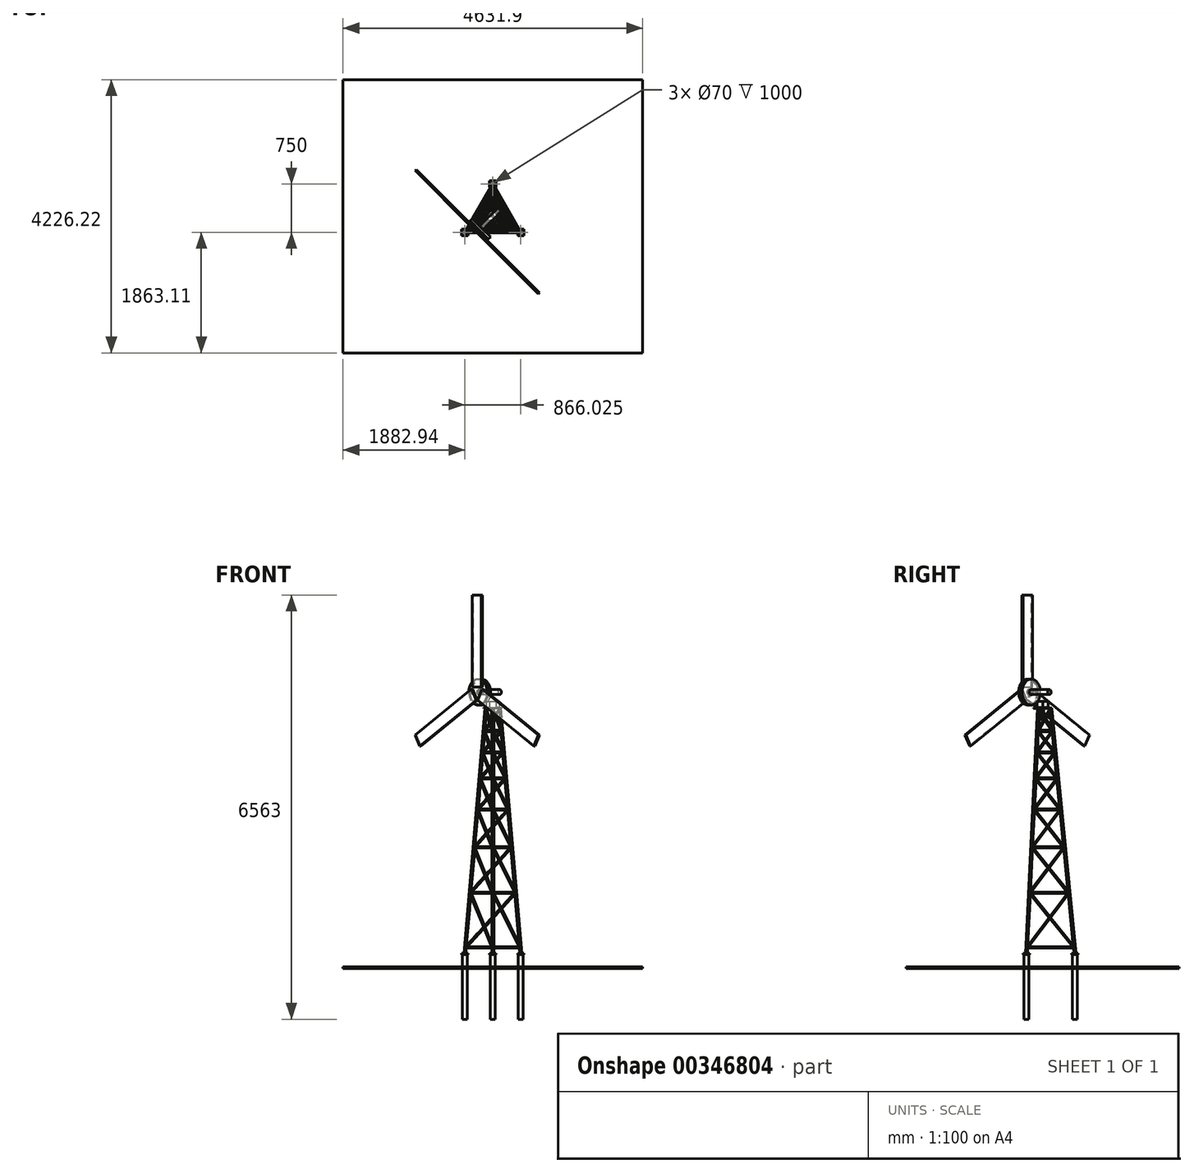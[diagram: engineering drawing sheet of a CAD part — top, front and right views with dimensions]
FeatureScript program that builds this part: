
annotation { "Feature Type Name" : "Feature", "Feature Type Description" : "" }
export const myFeature = defineFeature(function(context is Context, id is Id, definition is map)
    precondition{}
    {
        {
            assignVariable(context, id + "F0", {"name" : "RotorDia", "anyValue" : 3000});
        }
        {
            assignVariable(context, id + "F1", {"name" : "TowerHeight", "anyValue" : getVariable(context, 'RotorDia') / 2 + 2500});
        }
        {
            var Q0;
            Q0=qCreatedBy(makeId("Top.planeOp"),FACE);
            cPlane(context, id + "F2", {"entities" : qUnion([Q0]), "cplaneType" : CPlaneType.OFFSET, "offset" : 200 * mm, "width" : 150 * mm, "height" : 150 * mm});
        }
        {
            var Q0;
            Q0=qCreatedBy(id+"F2.planeOp",FACE);
            var sketch = newSketch(context, id + "F3", { "sketchPlane" : qUnion([Q0])});
            skLineSegment(sketch, "E0", {"start": v(0, 500) * mm, "end": v(-433.01, -250) * mm});
            skLineSegment(sketch, "E1", {"start": v(-433.01, -250) * mm, "end": v(433.01, -250) * mm});
            skLineSegment(sketch, "E2", {"start": v(433.01, -250) * mm, "end": v(0, 500) * mm});
            skLineSegment(sketch, "E3", {"start": v(-433.01, -250) * mm, "end": v(0, 0) * mm, "construction": true});
            skLineSegment(sketch, "E4", {"start": v(0, 0) * mm, "end": v(0, 500) * mm, "construction": true});
            skLineSegment(sketch, "E5", {"start": v(0, 0) * mm, "end": v(433.01, -250) * mm, "construction": true});
            skSolve(sketch);
        }
        {
            var Q0;
            Q0=qCreatedBy(makeId("Top.planeOp"),FACE);
            cPlane(context, id + "F4", {"entities" : qUnion([Q0]), "cplaneType" : CPlaneType.OFFSET, "offset" : (getVariable(context, 'TowerHeight')) * mm, "width" : 150 * mm, "height" : 150 * mm});
        }
        {
            var Q0;
            Q0=qCreatedBy(id+"F4.planeOp",FACE);
            var sketch = newSketch(context, id + "F5", { "sketchPlane" : qUnion([Q0])});
            skLineSegment(sketch, "E6", {"start": v(0, 125) * mm, "end": v(-108.25, -62.5) * mm});
            skLineSegment(sketch, "E7", {"start": v(-108.25, -62.5) * mm, "end": v(108.25, -62.5) * mm});
            skLineSegment(sketch, "E8", {"start": v(108.25, -62.5) * mm, "end": v(0, 125) * mm});
            skLineSegment(sketch, "E9", {"start": v(0, 125) * mm, "end": v(0, 0) * mm, "construction": true});
            skLineSegment(sketch, "E10", {"start": v(0, 0) * mm, "end": v(-108.25, -62.5) * mm, "construction": true});
            skLineSegment(sketch, "E11", {"start": v(108.25, -62.5) * mm, "end": v(0, 0) * mm, "construction": true});
            skSolve(sketch);
        }
        {
            var Q0;
            Q0=sQuery(id+"F3.wireOp",VERTEX,"E3.start");
            var Q1;
            Q1=sQuery(id+"F3.wireOp",VERTEX,"E5.end");
            var Q2;
            Q2=sQuery(id+"F5.wireOp",VERTEX,"E10.end");
            cPlane(context, id + "F6", {"entities" : qUnion([Q0, Q1, Q2]), "cplaneType" : CPlaneType.THREE_POINT, "offset" : 25 * mm, "width" : 150 * mm, "height" : 150 * mm});
        }
        {
            var Q0;
            Q0=qCreatedBy(id+"F6.planeOp",FACE);
            var sketch = newSketch(context, id + "F7", { "sketchPlane" : qUnion([Q0])});
            skLineSegment(sketch, "E12", {"start": v(433.01, 187.44) * mm, "end": v(108.25, 3992.06) * mm});
            skSolve(sketch);
        }
        {
            assignVariable(context, id + "F8", {"name" : "PipeThickness", "anyValue" : 3});
        }
        {
            var Q0;
            Q0=sQuery(id+"F7.wireOp",VERTEX,"E12.end");
            var Q1;
            Q1=sQuery(id+"F7.wireOp",EDGE,"E12");
            cPlane(context, id + "F9", {"entities" : qUnion([Q0, Q1]), "cplaneType" : CPlaneType.LINE_POINT, "offset" : 25 * mm, "width" : 150 * mm, "height" : 150 * mm});
        }
        {
            var Q0;
            Q0=qCreatedBy(id+"F9.planeOp",FACE);
            var sketch = newSketch(context, id + "F10", { "sketchPlane" : qUnion([Q0])});
            skCircle(sketch, "E13", {"center": v(-447.39, -259.55) * mm, "radius": 15 * mm});
            skSolve(sketch);
        }
        {
            var Q0;
            Q0=makeQuery(id+"F10.imprint","IMPRINT",FACE,{"disambiguationData":[TD([[makeQuery(id+"F10.imprint","IMPRINT",EDGE,{"derivedFrom":sQuery(id+"F10.wireOp",EDGE,"E13")}),1.0]])]});
            var Q1;
            Q1=sQuery(id+"F7.wireOp",EDGE,"E12");
            sweep(context, id + "F11", {"profiles" : qUnion([Q0]), "path" : qUnion([Q1])});
        }
        {
            var Q0;
            Q0=makeQuery(id+"F11.opSweep","CAP_FACE",FACE,{"disambiguationData":[OSD([sQuery(id+"F7.wireOp",VERTEX,"E12.end"),sQuery(id+"F10.wireOp",EDGE,"E13")])],"isStart":true});
            shell(context, id + "F12", {"entities" : qUnion([Q0]), "thickness" : (getVariable(context, 'PipeThickness')) * mm});
        }
        {
            var Q0;
            Q0=qCreatedBy(makeId("Front.planeOp"),FACE);
            var sketch = newSketch(context, id + "F13", { "sketchPlane" : qUnion([Q0])});
            skLineSegment(sketch, "E14", {"start": v(0, 0) * mm, "end": v(0, 4000) * mm});
            skSolve(sketch);
        }
        {
            var Q0;
            Q0=makeQuery(id+"F11.opSweep","SWEPT_BODY",BODY,{"disambiguationData":[OSD([sQuery(id+"F7.wireOp",EDGE,"E12"),sQuery(id+"F10.wireOp",EDGE,"E13")])]});
            var Q1;
            Q1=sQuery(id+"F13.wireOp",EDGE,"E14");
            transform(context, id + "F14", {"entities" : qUnion([Q0]), "transformType" : TransformType.ROTATION, "transformAxis" : qUnion([Q1]), "angle" : 120 * degree, "makeCopy" : true});
        }
        {
            var Q0;
            Q0=makeQuery(id+"F14.opPattern","COPY",BODY,{"derivedFrom":makeQuery(id+"F11.opSweep","SWEPT_BODY",BODY,{"disambiguationData":[OSD([sQuery(id+"F7.wireOp",EDGE,"E12"),sQuery(id+"F10.wireOp",EDGE,"E13")])]}),"instanceName":"1"});
            var Q1;
            Q1=sQuery(id+"F13.wireOp",EDGE,"E14");
            transform(context, id + "F15", {"entities" : qUnion([Q0]), "transformType" : TransformType.ROTATION, "transformAxis" : qUnion([Q1]), "angle" : 120 * degree, "makeCopy" : true});
        }
        {
            var Q0;
            Q0=qCreatedBy(id+"F4.planeOp",FACE);
            var sketch = newSketch(context, id + "F16", { "sketchPlane" : qUnion([Q0])});
            skCircle(sketch, "E15", {"center": v(0, 0) * mm, "radius": 139.93 * mm});
            skSolve(sketch);
        }
        {
            var Q0;
            Q0 = qSketchRegion(id + "F16", true);
            extrude(context, id + "F17", {"entities" : qUnion([Q0]), "depth" : 8 * mm});
        }
        {
            var Q0;
            Q0=makeQuery(id+"F17.opExtrude","CAP_FACE",FACE,{"disambiguationData":[OSD([sQuery(id+"F16.wireOp",EDGE,"E15")])],"isStart":false});
            var sketch = newSketch(context, id + "F18", { "sketchPlane" : qUnion([Q0])});
            skCircle(sketch, "E16", {"center": v(0, 0) * mm, "radius": 75 * mm});
            skCircle(sketch, "E17", {"center": v(0, 0) * mm, "radius": 80 * mm});
            skCircle(sketch, "E18", {"center": v(0, 0) * mm, "radius": 85 * mm});
            skCircle(sketch, "E19", {"center": v(0, 0) * mm, "radius": 90 * mm});
            skCircle(sketch, "E20", {"center": v(0, 0) * mm, "radius": 95 * mm});
            skCircle(sketch, "E21", {"center": v(0, 0) * mm, "radius": 100 * mm});
            skSolve(sketch);
        }
        {
            var Q0;
            Q0 = qSketchRegion(id + "F18", true);
            var Q1;
            Q1=makeQuery(id+"F18.imprint","IMPRINT",FACE,{"disambiguationData":[TD([[makeQuery(id+"F18.imprint","IMPRINT",EDGE,{"derivedFrom":sQuery(id+"F18.wireOp",EDGE,"E18")}),-1.0]])]});
            var Q2;
            Q2=makeQuery(id+"F18.imprint","IMPRINT",FACE,{"disambiguationData":[TD([[makeQuery(id+"F18.imprint","IMPRINT",EDGE,{"derivedFrom":sQuery(id+"F18.wireOp",EDGE,"E16")}),-1.0]])]});
            extrude(context, id + "F19", {"entities" : qUnion([Q0, Q1, Q2]), "depth" : 3 * mm});
        }
        {
            var Q0;
            Q0=makeQuery(id+"F17.opExtrude","CAP_FACE",FACE,{"disambiguationData":[OSD([sQuery(id+"F16.wireOp",EDGE,"E15")])],"isStart":false});
            var sketch = newSketch(context, id + "F20", { "sketchPlane" : qUnion([Q0])});
            skCircle(sketch, "E22", {"center": v(0, 0) * mm, "radius": 17.5 * mm});
            skSolve(sketch);
        }
        {
            var Q0;
            Q0 = qSketchRegion(id + "F20", true);
            extrude(context, id + "F21", {"entities" : qUnion([Q0]), "depth" : 25 * mm, "hasSecondDirection" : true, "secondDirectionOppositeDirection" : true, "secondDirectionDepth" : 200 * mm});
        }
        {
            var Q0;
            Q0=makeQuery(id+"F21.opExtrude","CAP_FACE",FACE,{"disambiguationData":[OSD([sQuery(id+"F20.wireOp",EDGE,"E22")])],"isStart":false});
            var sketch = newSketch(context, id + "F22", { "sketchPlane" : qUnion([Q0])});
            skCircle(sketch, "E23", {"center": v(0, 0) * mm, "radius": 60 * mm});
            skSolve(sketch);
        }
        {
            var Q0;
            Q0 = qSketchRegion(id + "F22", true);
            extrude(context, id + "F23", {"entities" : qUnion([Q0]), "operationType" : NewBodyOperationType.ADD, "depth" : 10 * mm});
        }
        {
            var Q0;
            Q0=makeQuery(id+"F23.opExtrude","CAP_FACE",FACE,{"disambiguationData":[OSD([sQuery(id+"F22.wireOp",EDGE,"E23")])],"isStart":false});
            var sketch = newSketch(context, id + "F24", { "sketchPlane" : qUnion([Q0])});
            skCircle(sketch, "E24.0", {"center": v(0, 0) * mm, "radius": 60 * mm});
            skSolve(sketch);
        }
        {
            var Q0;
            Q0 = qSketchRegion(id + "F24", true);
            extrude(context, id + "F25", {"entities" : qUnion([Q0]), "depth" : 10 * mm});
        }
        {
            var Q0;
            Q0=makeQuery(id+"F25.opExtrude","CAP_FACE",FACE,{"disambiguationData":[OSD([sQuery(id+"F24.wireOp",EDGE,"E24.0")])],"isStart":false});
            var sketch = newSketch(context, id + "F26", { "sketchPlane" : qUnion([Q0])});
            skPoint(sketch, "E25", {"position": v(0, 50) * mm});
            skPoint(sketch, "E26.1.0", {"position": v(-50, 0) * mm});
            skPoint(sketch, "E26.2.0", {"position": v(0, -50) * mm});
            skPoint(sketch, "E26.3.0", {"position": v(50, 0) * mm});
            skPoint(sketch, "E26.center", {"position": v(0, 0) * mm});
            skSolve(sketch);
        }
        {
            var Q0;
            Q0=sQuery(id+"F26.wireOp",VERTEX,"E25");
            var Q1;
            Q1=sQuery(id+"F26.wireOp",VERTEX,"E26.3.0");
            var Q2;
            Q2=sQuery(id+"F26.wireOp",VERTEX,"E26.2.0");
            var Q3;
            Q3=sQuery(id+"F26.wireOp",VERTEX,"E26.1.0");
            var Q4;
            Q4=makeQuery(id+"F25.opExtrude","SWEPT_BODY",BODY,{"disambiguationData":[OSD([sQuery(id+"F24.wireOp",EDGE,"E24.0")])]});
            var Q5;
            Q5=makeQuery(id+"F21.opExtrude","SWEPT_BODY",BODY,{"disambiguationData":[OSD([sQuery(id+"F20.wireOp",EDGE,"E22")])]});
            hole(context, id + "F27", {"style" : HoleStyle.SIMPLE, "endStyle" : HoleEndStyle.THROUGH, "standardTappedOrClearance" : lookupTablePath({ "standard" : "ISO", "fit" : "Close", "size" : "M12", "type" : "Clearance" }), "standardBlindInLast" : lookupTablePath({ "fit" : "Close", "standard" : "ISO", "size" : "M12", "type" : "Clearance" }), "holeDiameter" : 12.6 * mm, "isTappedThrough" : true, "tappedDepth" : 12 * mm, "tapClearance" : 3, "locations" : qUnion([Q0, Q1, Q2, Q3]), "scope" : qUnion([Q4, Q5])});
        }
        {
            var Q0;
            Q0=qCreatedBy(makeId("Front.planeOp"),FACE);
            var Q1;
            Q1=qCreatedBy(makeId("Right.planeOp"),FACE);
            cPlane(context, id + "F28", {"entities" : qUnion([Q0, Q1]), "cplaneType" : CPlaneType.MID_PLANE, "offset" : 25 * mm, "width" : 150 * mm, "height" : 150 * mm});
        }
        {
            var Q0;
            Q0=qCreatedBy(id+"F28.planeOp",FACE);
            var sketch = newSketch(context, id + "F29", { "sketchPlane" : qUnion([Q0])});
            skCircle(sketch, "E27", {"center": v(0, 4253) * mm, "radius": 38 * mm});
            skSolve(sketch);
        }
        {
            var Q0;
            Q0 = qSketchRegion(id + "F29", true);
            extrude(context, id + "F30", {"entities" : qUnion([Q0]), "depth" : 300 * mm, "hasSecondDirection" : true, "secondDirectionOppositeDirection" : true, "secondDirectionDepth" : 150 * mm});
        }
        {
            var Q0;
            Q0=makeQuery(id+"F30.opExtrude","CAP_FACE",FACE,{"disambiguationData":[OSD([sQuery(id+"F29.wireOp",EDGE,"E27")])],"isStart":false});
            var sketch = newSketch(context, id + "F31", { "sketchPlane" : qUnion([Q0])});
            skCircle(sketch, "E28", {"center": v(0, 4253) * mm, "radius": 200 * mm});
            skSolve(sketch);
        }
        {
            var Q0;
            Q0 = qSketchRegion(id + "F31", true);
            extrude(context, id + "F32", {"entities" : qUnion([Q0]), "depth" : 25 * mm});
        }
        {
            var Q0;
            Q0=makeQuery(id+"F32.opExtrude","CAP_FACE",FACE,{"disambiguationData":[OSD([sQuery(id+"F31.wireOp",EDGE,"E28")])],"isStart":true});
            cPlane(context, id + "F33", {"entities" : qUnion([Q0]), "cplaneType" : CPlaneType.OFFSET, "offset" : 1 * mm, "width" : 150 * mm, "height" : 150 * mm});
        }
        {
            var Q0;
            Q0=qCreatedBy(id+"F33.planeOp",FACE);
            var sketch = newSketch(context, id + "F34", { "sketchPlane" : qUnion([Q0])});
            skCircle(sketch, "E29.0", {"center": v(0, 4253) * mm, "radius": 200 * mm});
            skCircle(sketch, "E30", {"center": v(0, 4253) * mm, "radius": 43 * mm});
            skCircle(sketch, "E31.0", {"center": v(0, 4253) * mm, "radius": 38 * mm, "construction": true});
            skSolve(sketch);
        }
        {
            var Q0;
            Q0 = qSketchRegion(id + "F34", true);
            extrude(context, id + "F35", {"entities" : qUnion([Q0]), "depth" : 50 * mm});
        }
        {
            var Q0;
            Q0=makeQuery(id+"F32.opExtrude","CAP_FACE",FACE,{"disambiguationData":[OSD([sQuery(id+"F31.wireOp",EDGE,"E28")])],"isStart":false});
            var sketch = newSketch(context, id + "F36", { "sketchPlane" : qUnion([Q0])});
            skLineSegment(sketch, "E32", {"start": v(0, 4253) * mm, "end": v(0, 6624.87) * mm, "construction": true});
            skLineSegment(sketch, "E33.bottom", {"start": v(100, 4328) * mm, "end": v(-100, 4328) * mm});
            skLineSegment(sketch, "E33.top", {"start": v(100, 5753) * mm, "end": v(-100, 5753) * mm});
            skLineSegment(sketch, "E33.left", {"start": v(100, 4328) * mm, "end": v(100, 5753) * mm});
            skLineSegment(sketch, "E33.right", {"start": v(-100, 4328) * mm, "end": v(-100, 5753) * mm});
            skPoint(sketch, "E33.middle", {"position": v(0, 5040.5) * mm});
            skLineSegment(sketch, "E34.1.0", {"start": v(-114.95, 4302.1) * mm, "end": v(-14.95, 4128.9) * mm});
            skLineSegment(sketch, "E34.1.1", {"start": v(-114.95, 4302.1) * mm, "end": v(-1349.04, 3589.6) * mm});
            skLineSegment(sketch, "E34.1.2", {"start": v(-1349.04, 3589.6) * mm, "end": v(-1249.04, 3416.4) * mm});
            skLineSegment(sketch, "E34.1.3", {"start": v(-14.95, 4128.9) * mm, "end": v(-1249.04, 3416.4) * mm});
            skPoint(sketch, "E34.1.4", {"position": v(-682, 3859.25) * mm});
            skLineSegment(sketch, "E34.2.0", {"start": v(14.95, 4128.9) * mm, "end": v(114.95, 4302.1) * mm});
            skLineSegment(sketch, "E34.2.1", {"start": v(14.95, 4128.9) * mm, "end": v(1249.04, 3416.4) * mm});
            skLineSegment(sketch, "E34.2.2", {"start": v(1249.04, 3416.4) * mm, "end": v(1349.04, 3589.6) * mm});
            skLineSegment(sketch, "E34.2.3", {"start": v(114.95, 4302.1) * mm, "end": v(1349.04, 3589.6) * mm});
            skPoint(sketch, "E34.2.4", {"position": v(682, 3859.25) * mm});
            skPoint(sketch, "E34.center", {"position": v(0, 4253) * mm});
            skSolve(sketch);
        }
        {
            var Q0;
            Q0 = qSketchRegion(id + "F36", true);
            extrude(context, id + "F37", {"entities" : qUnion([Q0]), "depth" : 25 * mm});
        }
        {
            var Q0;
            Q0=qCreatedBy(makeId("Top.planeOp"),FACE);
            var sketch = newSketch(context, id + "F38", { "sketchPlane" : qUnion([Q0])});
            skLineSegment(sketch, "E35.bottom", {"start": v(2315.95, -2113.11) * mm, "end": v(-2315.95, -2113.11) * mm});
            skLineSegment(sketch, "E35.top", {"start": v(2315.95, 2113.11) * mm, "end": v(-2315.95, 2113.11) * mm});
            skLineSegment(sketch, "E35.left", {"start": v(2315.95, -2113.11) * mm, "end": v(2315.95, 2113.11) * mm});
            skLineSegment(sketch, "E35.right", {"start": v(-2315.95, -2113.11) * mm, "end": v(-2315.95, 2113.11) * mm});
            skPoint(sketch, "E35.middle", {"position": v(0, 0) * mm});
            skSolve(sketch);
        }
        {
            var Q0;
            Q0 = qSketchRegion(id + "F38", true);
            extrude(context, id + "F39", {"entities" : qUnion([Q0]), "oppositeDirection" : true, "depth" : 25 * mm});
        }
        {
            var Q0;
            Q0=qCreatedBy(id+"F2.planeOp",FACE);
            var sketch = newSketch(context, id + "F40", { "sketchPlane" : qUnion([Q0])});
            skLineSegment(sketch, "E36.bottom", {"start": v(383.01, -300) * mm, "end": v(483.01, -300) * mm});
            skLineSegment(sketch, "E36.top", {"start": v(383.01, -200) * mm, "end": v(483.01, -200) * mm});
            skLineSegment(sketch, "E36.left", {"start": v(383.01, -300) * mm, "end": v(383.01, -200) * mm});
            skLineSegment(sketch, "E36.right", {"start": v(483.01, -300) * mm, "end": v(483.01, -200) * mm});
            skPoint(sketch, "E36.middle", {"position": v(433.01, -250) * mm});
            skLineSegment(sketch, "E37.bottom", {"start": v(-483.01, -300) * mm, "end": v(-383.01, -300) * mm});
            skLineSegment(sketch, "E37.top", {"start": v(-483.01, -200) * mm, "end": v(-383.01, -200) * mm});
            skLineSegment(sketch, "E37.left", {"start": v(-483.01, -300) * mm, "end": v(-483.01, -200) * mm});
            skLineSegment(sketch, "E37.right", {"start": v(-383.01, -300) * mm, "end": v(-383.01, -200) * mm});
            skPoint(sketch, "E37.middle", {"position": v(-433.01, -250) * mm});
            skLineSegment(sketch, "E38.bottom", {"start": v(-50, 450) * mm, "end": v(50, 450) * mm});
            skLineSegment(sketch, "E38.top", {"start": v(-50, 550) * mm, "end": v(50, 550) * mm});
            skLineSegment(sketch, "E38.left", {"start": v(-50, 450) * mm, "end": v(-50, 550) * mm});
            skLineSegment(sketch, "E38.right", {"start": v(50, 450) * mm, "end": v(50, 550) * mm});
            skPoint(sketch, "E38.middle", {"position": v(0, 500) * mm});
            skSolve(sketch);
        }
        {
            var Q0;
            Q0 = qSketchRegion(id + "F40", true);
            extrude(context, id + "F41", {"entities" : qUnion([Q0]), "depth" : 10 * mm});
        }
        {
            var Q0;
            Q0=makeQuery(id+"F41.opExtrude","CAP_FACE",FACE,{"disambiguationData":[OSD([sQuery(id+"F40.wireOp",EDGE,"E38.bottom"),sQuery(id+"F40.wireOp",EDGE,"E38.top"),sQuery(id+"F40.wireOp",EDGE,"E38.left"),sQuery(id+"F40.wireOp",EDGE,"E38.right")])],"isStart":true});
            var sketch = newSketch(context, id + "F42", { "sketchPlane" : qUnion([Q0])});
            skLineSegment(sketch, "E39.0.0", {"start": v(-50, -550) * mm, "end": v(50, -550) * mm});
            skLineSegment(sketch, "E39.0.1", {"start": v(50, -550) * mm, "end": v(50, -450) * mm});
            skLineSegment(sketch, "E39.0.2", {"start": v(50, -450) * mm, "end": v(-50, -450) * mm});
            skLineSegment(sketch, "E39.0.3", {"start": v(-50, -450) * mm, "end": v(-50, -550) * mm});
            skLineSegment(sketch, "E40.0.0", {"start": v(383.01, 200) * mm, "end": v(483.01, 200) * mm});
            skLineSegment(sketch, "E40.0.1", {"start": v(483.01, 200) * mm, "end": v(483.01, 300) * mm});
            skLineSegment(sketch, "E40.0.2", {"start": v(483.01, 300) * mm, "end": v(383.01, 300) * mm});
            skLineSegment(sketch, "E40.0.3", {"start": v(383.01, 300) * mm, "end": v(383.01, 200) * mm});
            skLineSegment(sketch, "E41.0.0", {"start": v(-483.01, 200) * mm, "end": v(-383.01, 200) * mm});
            skLineSegment(sketch, "E41.0.1", {"start": v(-383.01, 200) * mm, "end": v(-383.01, 300) * mm});
            skLineSegment(sketch, "E41.0.2", {"start": v(-383.01, 300) * mm, "end": v(-483.01, 300) * mm});
            skLineSegment(sketch, "E41.0.3", {"start": v(-483.01, 300) * mm, "end": v(-483.01, 200) * mm});
            skSolve(sketch);
        }
        {
            var Q0;
            Q0 = qSketchRegion(id + "F42", true);
            extrude(context, id + "F43", {"entities" : qUnion([Q0]), "depth" : 10 * mm});
        }
        {
            var Q0;
            Q0=makeQuery(id+"F43.opExtrude","CAP_FACE",FACE,{"disambiguationData":[OSD([sQuery(id+"F42.wireOp",EDGE,"E39.0.0"),sQuery(id+"F42.wireOp",EDGE,"E39.0.1"),sQuery(id+"F42.wireOp",EDGE,"E39.0.2"),sQuery(id+"F42.wireOp",EDGE,"E39.0.3")])],"isStart":false});
            var sketch = newSketch(context, id + "F44", { "sketchPlane" : qUnion([Q0])});
            skCircle(sketch, "E42", {"center": v(0, -500) * mm, "radius": 38 * mm});
            skCircle(sketch, "E43", {"center": v(433.01, 250) * mm, "radius": 38 * mm});
            skCircle(sketch, "E44", {"center": v(-433.01, 250) * mm, "radius": 38 * mm});
            skCircle(sketch, "E45", {"center": v(0, -500) * mm, "radius": 35 * mm});
            skCircle(sketch, "E46", {"center": v(433.01, 250) * mm, "radius": 35 * mm});
            skCircle(sketch, "E47", {"center": v(-433.01, 250) * mm, "radius": 35 * mm});
            skSolve(sketch);
        }
        {
            var Q0;
            Q0 = qSketchRegion(id + "F44", true);
            extrude(context, id + "F45", {"entities" : qUnion([Q0]), "depth" : 1000 * mm});
        }
        {
            var Q0;
            Q0=qCreatedBy(id+"F6.planeOp",FACE);
            var sketch = newSketch(context, id + "F46", { "sketchPlane" : qUnion([Q0])});
            skLineSegment(sketch, "E48", {"start": v(433.01, 194.96) * mm, "end": v(108.25, 3992.06) * mm, "construction": true});
            skLineSegment(sketch, "E49", {"start": v(-433.01, 184.97) * mm, "end": v(-108.25, 3992.06) * mm, "construction": true});
            skLineSegment(sketch, "E50", {"start": v(425.1, 287.44) * mm, "end": v(-424.27, 287.44) * mm, "construction": true});
            skLineSegment(sketch, "E51", {"start": v(352.46, 1136.81) * mm, "end": v(-351.82, 1136.81) * mm, "construction": true});
            skLineSegment(sketch, "E52", {"start": v(292.22, 1841.09) * mm, "end": v(-291.74, 1841.09) * mm, "construction": true});
            skLineSegment(sketch, "E53", {"start": v(242.28, 2425.05) * mm, "end": v(-241.93, 2425.05) * mm, "construction": true});
            skLineSegment(sketch, "E54", {"start": v(200.86, 2909.25) * mm, "end": v(-200.62, 2909.25) * mm, "construction": true});
            skLineSegment(sketch, "E55", {"start": v(166.53, 3310.74) * mm, "end": v(-166.37, 3310.74) * mm, "construction": true});
            skLineSegment(sketch, "E56", {"start": v(138.05, 3643.63) * mm, "end": v(-137.98, 3643.63) * mm, "construction": true});
            skLineSegment(sketch, "E57", {"start": v(144.63, 287.44) * mm, "end": v(144.63, 1136.81) * mm, "construction": true});
            skLineSegment(sketch, "E58", {"start": v(-119.67, 1136.81) * mm, "end": v(-119.67, 1841.09) * mm, "construction": true});
            skLineSegment(sketch, "E59", {"start": v(112.4, 1841.09) * mm, "end": v(112.4, 2425.05) * mm, "construction": true});
            skLineSegment(sketch, "E60", {"start": v(-67.21, 2425.05) * mm, "end": v(-67.21, 2909.25) * mm, "construction": true});
            skLineSegment(sketch, "E61", {"start": v(72.8, 2909.25) * mm, "end": v(72.8, 3310.74) * mm, "construction": true});
            skLineSegment(sketch, "E62", {"start": v(-67.21, 3310.74) * mm, "end": v(-67.21, 3643.63) * mm, "construction": true});
            skSolve(sketch);
        }
        {
            var Q0;
            Q0=qCreatedBy(makeId("Right.planeOp"),FACE);
            var sketch = newSketch(context, id + "F47", { "sketchPlane" : qUnion([Q0])});
            skCircle(sketch, "E63", {"center": v(-245.07, 299.88) * mm, "radius": 10 * mm});
            skCircle(sketch, "E64", {"center": v(-203.21, 1148.22) * mm, "radius": 10 * mm});
            skCircle(sketch, "E65", {"center": v(-168.5, 1851.64) * mm, "radius": 10 * mm});
            skCircle(sketch, "E66", {"center": v(-139.73, 2434.9) * mm, "radius": 10 * mm});
            skCircle(sketch, "E67", {"center": v(-115.86, 2918.5) * mm, "radius": 10 * mm});
            skLineSegment(sketch, "E68", {"start": v(-250, 200) * mm, "end": v(-62.5, 4000) * mm, "construction": true});
            skCircle(sketch, "E69", {"center": v(-96.08, 3319.5) * mm, "radius": 10 * mm});
            skCircle(sketch, "E70", {"center": v(-79.67, 3652) * mm, "radius": 10 * mm});
            skCircle(sketch, "E71", {"center": v(-79.67, 3652) * mm, "radius": 8 * mm});
            skCircle(sketch, "E72", {"center": v(-96.08, 3319.5) * mm, "radius": 8 * mm});
            skCircle(sketch, "E73", {"center": v(-115.86, 2918.5) * mm, "radius": 8 * mm});
            skCircle(sketch, "E74", {"center": v(-139.73, 2434.9) * mm, "radius": 8 * mm});
            skCircle(sketch, "E75", {"center": v(-168.5, 1851.64) * mm, "radius": 8 * mm});
            skCircle(sketch, "E76", {"center": v(-203.21, 1148.22) * mm, "radius": 8 * mm});
            skCircle(sketch, "E77", {"center": v(-245.07, 299.88) * mm, "radius": 8 * mm});
            skSolve(sketch);
        }
        {
            var Q0;
            Q0 = qSketchRegion(id + "F47", true);
            extrude(context, id + "F48", {"entities" : qUnion([Q0]), "endBound" : BoundingType.UP_TO_NEXT, "depth" : 25 * mm, "hasSecondDirection" : true, "secondDirectionBound" : SecondDirectionBoundingType.UP_TO_NEXT, "secondDirectionOppositeDirection" : true, "secondDirectionDepth" : 25 * mm});
        }
        {
            var Q0;
            Q0=qCreatedBy(id+"F6.planeOp",FACE);
            var sketch = newSketch(context, id + "F49", { "sketchPlane" : qUnion([Q0])});
            skLineSegment(sketch, "E78", {"start": v(-337.77, 1126.81) * mm, "end": v(408.57, 297.44) * mm, "construction": true});
            skLineSegment(sketch, "E79", {"start": v(408.57, 297.44) * mm, "end": v(-71.24, 830.63) * mm});
            skSolve(sketch);
        }
        {
            var Q0;
            Q0=sQuery(id+"F49.wireOp",EDGE,"E79");
            var Q1;
            Q1=sQuery(id+"F49.wireOp",VERTEX,"E79.end");
            cPlane(context, id + "F50", {"entities" : qUnion([Q0, Q1]), "cplaneType" : CPlaneType.LINE_POINT, "offset" : 25 * mm, "width" : 150 * mm, "height" : 150 * mm});
        }
        {
            var Q0;
            Q0=qCreatedBy(id+"F50.planeOp",FACE);
            var sketch = newSketch(context, id + "F51", { "sketchPlane" : qUnion([Q0])});
            skCircle(sketch, "E80", {"center": v(-502.66, -259.55) * mm, "radius": 10 * mm});
            skCircle(sketch, "E81", {"center": v(-502.66, -259.55) * mm, "radius": 8 * mm});
            skSolve(sketch);
        }
        {
            var Q0;
            Q0 = qSketchRegion(id + "F51", true);
            var Q1;
            Q1=makeQuery(id+"F14.opPattern","COPY",BODY,{"derivedFrom":makeQuery(id+"F11.opSweep","SWEPT_BODY",BODY,{"disambiguationData":[OSD([sQuery(id+"F7.wireOp",EDGE,"E12"),sQuery(id+"F10.wireOp",EDGE,"E13")])]}),"instanceName":"1"});
            var Q2;
            Q2=makeQuery(id+"F11.opSweep","SWEPT_BODY",BODY,{"disambiguationData":[OSD([sQuery(id+"F7.wireOp",EDGE,"E12"),sQuery(id+"F10.wireOp",EDGE,"E13")])]});
            extrude(context, id + "F52", {"entities" : qUnion([Q0]), "endBound" : BoundingType.UP_TO_BODY, "endBoundEntityBody" : qUnion([Q1]), "depth" : 25 * mm, "hasSecondDirection" : true, "secondDirectionBound" : SecondDirectionBoundingType.UP_TO_BODY, "secondDirectionOppositeDirection" : true, "secondDirectionBoundEntityBody" : qUnion([Q2]), "secondDirectionDepth" : 25 * mm});
        }
        {
            var Q0;
            Q0=qCreatedBy(id+"F6.planeOp",FACE);
            var sketch = newSketch(context, id + "F53", { "sketchPlane" : qUnion([Q0])});
            skLineSegment(sketch, "E82", {"start": v(336.07, 1146.81) * mm, "end": v(-277.66, 1831.09) * mm, "construction": true});
            skLineSegment(sketch, "E83", {"start": v(336.07, 1146.81) * mm, "end": v(116.17, 1391.98) * mm});
            skSolve(sketch);
        }
        {
            var Q0;
            Q0=sQuery(id+"F53.wireOp",VERTEX,"E83.end");
            var Q1;
            Q1=sQuery(id+"F53.wireOp",EDGE,"E83");
            cPlane(context, id + "F54", {"entities" : qUnion([Q0, Q1]), "cplaneType" : CPlaneType.LINE_POINT, "offset" : 25 * mm, "width" : 150 * mm, "height" : 150 * mm});
        }
        {
            var Q0;
            Q0=qCreatedBy(id+"F54.planeOp",FACE);
            var sketch = newSketch(context, id + "F55", { "sketchPlane" : qUnion([Q0])});
            skCircle(sketch, "E84", {"center": v(-1015.9, -259.55) * mm, "radius": 10 * mm});
            skCircle(sketch, "E85", {"center": v(-1015.9, -259.55) * mm, "radius": 8 * mm});
            skSolve(sketch);
        }
        {
            var Q0;
            Q0 = qSketchRegion(id + "F55", true);
            var Q1;
            Q1=makeQuery(id+"F14.opPattern","COPY",BODY,{"derivedFrom":makeQuery(id+"F11.opSweep","SWEPT_BODY",BODY,{"disambiguationData":[OSD([sQuery(id+"F7.wireOp",EDGE,"E12"),sQuery(id+"F10.wireOp",EDGE,"E13")])]}),"instanceName":"1"});
            var Q2;
            Q2=makeQuery(id+"F11.opSweep","SWEPT_BODY",BODY,{"disambiguationData":[OSD([sQuery(id+"F7.wireOp",EDGE,"E12"),sQuery(id+"F10.wireOp",EDGE,"E13")])]});
            extrude(context, id + "F56", {"entities" : qUnion([Q0]), "endBound" : BoundingType.UP_TO_BODY, "endBoundEntityBody" : qUnion([Q1]), "depth" : 25 * mm, "hasSecondDirection" : true, "secondDirectionBound" : SecondDirectionBoundingType.UP_TO_BODY, "secondDirectionOppositeDirection" : true, "secondDirectionBoundEntityBody" : qUnion([Q2]), "secondDirectionDepth" : 25 * mm});
        }
        {
            var Q0;
            Q0=qCreatedBy(id+"F6.planeOp",FACE);
            var sketch = newSketch(context, id + "F57", { "sketchPlane" : qUnion([Q0])});
            skLineSegment(sketch, "E86", {"start": v(275.95, 1851.09) * mm, "end": v(-227.81, 2415.05) * mm, "construction": true});
            skLineSegment(sketch, "E87", {"start": v(275.95, 1851.09) * mm, "end": v(49.73, 2104.34) * mm});
            skSolve(sketch);
        }
        {
            var Q0;
            Q0=sQuery(id+"F57.wireOp",VERTEX,"E87.end");
            var Q1;
            Q1=sQuery(id+"F57.wireOp",EDGE,"E87");
            cPlane(context, id + "F58", {"entities" : qUnion([Q0, Q1]), "cplaneType" : CPlaneType.LINE_POINT, "offset" : 25 * mm, "width" : 150 * mm, "height" : 150 * mm});
        }
        {
            var Q0;
            Q0=qCreatedBy(id+"F58.planeOp",FACE);
            var sketch = newSketch(context, id + "F59", { "sketchPlane" : qUnion([Q0])});
            skCircle(sketch, "E88", {"center": v(-1438.96, -259.55) * mm, "radius": 10 * mm});
            skCircle(sketch, "E89", {"center": v(-1438.96, -259.55) * mm, "radius": 8 * mm});
            skSolve(sketch);
        }
        {
            var Q0;
            Q0 = qSketchRegion(id + "F59", true);
            var Q1;
            Q1=makeQuery(id+"F14.opPattern","COPY",BODY,{"derivedFrom":makeQuery(id+"F11.opSweep","SWEPT_BODY",BODY,{"disambiguationData":[OSD([sQuery(id+"F7.wireOp",EDGE,"E12"),sQuery(id+"F10.wireOp",EDGE,"E13")])]}),"instanceName":"1"});
            var Q2;
            Q2=makeQuery(id+"F11.opSweep","SWEPT_BODY",BODY,{"disambiguationData":[OSD([sQuery(id+"F7.wireOp",EDGE,"E12"),sQuery(id+"F10.wireOp",EDGE,"E13")])]});
            extrude(context, id + "F60", {"entities" : qUnion([Q0]), "endBound" : BoundingType.UP_TO_BODY, "endBoundEntityBody" : qUnion([Q1]), "depth" : 25 * mm, "hasSecondDirection" : true, "secondDirectionBound" : SecondDirectionBoundingType.UP_TO_BODY, "secondDirectionOppositeDirection" : true, "secondDirectionBoundEntityBody" : qUnion([Q2]), "secondDirectionDepth" : 25 * mm});
        }
        {
            var Q0;
            Q0=qCreatedBy(id+"F6.planeOp",FACE);
            var sketch = newSketch(context, id + "F61", { "sketchPlane" : qUnion([Q0])});
            skLineSegment(sketch, "E90", {"start": v(226.1, 2435.05) * mm, "end": v(-186.48, 2899.25) * mm, "construction": true});
            skLineSegment(sketch, "E91", {"start": v(226.1, 2435.05) * mm, "end": v(47.16, 2636.38) * mm});
            skSolve(sketch);
        }
        {
            var Q0;
            Q0=sQuery(id+"F61.wireOp",VERTEX,"E91.end");
            var Q1;
            Q1=sQuery(id+"F61.wireOp",EDGE,"E91");
            cPlane(context, id + "F62", {"entities" : qUnion([Q0, Q1]), "cplaneType" : CPlaneType.LINE_POINT, "offset" : 25 * mm, "width" : 150 * mm, "height" : 150 * mm});
        }
        {
            var Q0;
            Q0=qCreatedBy(id+"F62.planeOp",FACE);
            var sketch = newSketch(context, id + "F63", { "sketchPlane" : qUnion([Q0])});
            skCircle(sketch, "E92", {"center": v(-1786.67, -259.55) * mm, "radius": 10 * mm});
            skCircle(sketch, "E93", {"center": v(-1786.67, -259.55) * mm, "radius": 8 * mm});
            skSolve(sketch);
        }
        {
            var Q0;
            Q0 = qSketchRegion(id + "F63", true);
            var Q1;
            Q1=makeQuery(id+"F14.opPattern","COPY",BODY,{"derivedFrom":makeQuery(id+"F11.opSweep","SWEPT_BODY",BODY,{"disambiguationData":[OSD([sQuery(id+"F7.wireOp",EDGE,"E12"),sQuery(id+"F10.wireOp",EDGE,"E13")])]}),"instanceName":"1"});
            var Q2;
            Q2=makeQuery(id+"F11.opSweep","SWEPT_BODY",BODY,{"disambiguationData":[OSD([sQuery(id+"F7.wireOp",EDGE,"E12"),sQuery(id+"F10.wireOp",EDGE,"E13")])]});
            extrude(context, id + "F64", {"entities" : qUnion([Q0]), "endBound" : BoundingType.UP_TO_BODY, "endBoundEntityBody" : qUnion([Q1]), "depth" : 25 * mm, "hasSecondDirection" : true, "secondDirectionBound" : SecondDirectionBoundingType.UP_TO_BODY, "secondDirectionOppositeDirection" : true, "secondDirectionBoundEntityBody" : qUnion([Q2]), "secondDirectionDepth" : 25 * mm});
        }
        {
            var Q0;
            Q0=qCreatedBy(id+"F6.planeOp",FACE);
            var sketch = newSketch(context, id + "F65", { "sketchPlane" : qUnion([Q0])});
            skLineSegment(sketch, "E94", {"start": v(184.77, 2919.25) * mm, "end": v(-152.2, 3300.74) * mm, "construction": true});
            skLineSegment(sketch, "E95", {"start": v(184.77, 2919.25) * mm, "end": v(47.85, 3074.26) * mm});
            skSolve(sketch);
        }
        {
            var Q0;
            Q0=sQuery(id+"F65.wireOp",VERTEX,"E95.end");
            var Q1;
            Q1=sQuery(id+"F65.wireOp",EDGE,"E95");
            cPlane(context, id + "F66", {"entities" : qUnion([Q0, Q1]), "cplaneType" : CPlaneType.LINE_POINT, "offset" : 25 * mm, "width" : 150 * mm, "height" : 150 * mm});
        }
        {
            var Q0;
            Q0=qCreatedBy(id+"F66.planeOp",FACE);
            var sketch = newSketch(context, id + "F67", { "sketchPlane" : qUnion([Q0])});
            skCircle(sketch, "E96", {"center": v(-2071.14, -259.55) * mm, "radius": 10 * mm});
            skCircle(sketch, "E97", {"center": v(-2071.14, -259.55) * mm, "radius": 8 * mm});
            skSolve(sketch);
        }
        {
            var Q0;
            Q0 = qSketchRegion(id + "F67", true);
            var Q1;
            Q1=makeQuery(id+"F14.opPattern","COPY",BODY,{"derivedFrom":makeQuery(id+"F11.opSweep","SWEPT_BODY",BODY,{"disambiguationData":[OSD([sQuery(id+"F7.wireOp",EDGE,"E12"),sQuery(id+"F10.wireOp",EDGE,"E13")])]}),"instanceName":"1"});
            var Q2;
            Q2=makeQuery(id+"F11.opSweep","SWEPT_BODY",BODY,{"disambiguationData":[OSD([sQuery(id+"F7.wireOp",EDGE,"E12"),sQuery(id+"F10.wireOp",EDGE,"E13")])]});
            extrude(context, id + "F68", {"entities" : qUnion([Q0]), "endBound" : BoundingType.UP_TO_BODY, "endBoundEntityBody" : qUnion([Q1]), "depth" : 25 * mm, "hasSecondDirection" : true, "secondDirectionBound" : SecondDirectionBoundingType.UP_TO_BODY, "secondDirectionOppositeDirection" : true, "secondDirectionBoundEntityBody" : qUnion([Q2]), "secondDirectionDepth" : 25 * mm});
        }
        {
            var Q0;
            Q0=qCreatedBy(id+"F6.planeOp",FACE);
            var sketch = newSketch(context, id + "F69", { "sketchPlane" : qUnion([Q0])});
            skLineSegment(sketch, "E98", {"start": v(150.5, 3320.74) * mm, "end": v(-123.8, 3633.63) * mm, "construction": true});
            skLineSegment(sketch, "E99", {"start": v(150.5, 3320.74) * mm, "end": v(34.32, 3453.27) * mm});
            skSolve(sketch);
        }
        {
            var Q0;
            Q0=sQuery(id+"F69.wireOp",VERTEX,"E99.end");
            var Q1;
            Q1=sQuery(id+"F69.wireOp",EDGE,"E99");
            cPlane(context, id + "F70", {"entities" : qUnion([Q0, Q1]), "cplaneType" : CPlaneType.LINE_POINT, "offset" : 25 * mm, "width" : 150 * mm, "height" : 150 * mm});
        }
        {
            var Q0;
            Q0=qCreatedBy(id+"F70.planeOp",FACE);
            var sketch = newSketch(context, id + "F71", { "sketchPlane" : qUnion([Q0])});
            skCircle(sketch, "E100", {"center": v(-2302.2, -259.55) * mm, "radius": 10 * mm});
            skCircle(sketch, "E101", {"center": v(-2302.2, -259.55) * mm, "radius": 8 * mm});
            skSolve(sketch);
        }
        {
            var Q0;
            Q0 = qSketchRegion(id + "F71", true);
            var Q1;
            Q1=makeQuery(id+"F14.opPattern","COPY",BODY,{"derivedFrom":makeQuery(id+"F11.opSweep","SWEPT_BODY",BODY,{"disambiguationData":[OSD([sQuery(id+"F7.wireOp",EDGE,"E12"),sQuery(id+"F10.wireOp",EDGE,"E13")])]}),"instanceName":"1"});
            var Q2;
            Q2=makeQuery(id+"F11.opSweep","SWEPT_BODY",BODY,{"disambiguationData":[OSD([sQuery(id+"F7.wireOp",EDGE,"E12"),sQuery(id+"F10.wireOp",EDGE,"E13")])]});
            extrude(context, id + "F72", {"entities" : qUnion([Q0]), "endBound" : BoundingType.UP_TO_BODY, "endBoundEntityBody" : qUnion([Q1]), "depth" : 25 * mm, "hasSecondDirection" : true, "secondDirectionBound" : SecondDirectionBoundingType.UP_TO_BODY, "secondDirectionOppositeDirection" : true, "secondDirectionBoundEntityBody" : qUnion([Q2]), "secondDirectionDepth" : 25 * mm});
        }
        {
            var Q0;
            Q0=qCreatedBy(id+"F6.planeOp",FACE);
            var sketch = newSketch(context, id + "F73", { "sketchPlane" : qUnion([Q0])});
            skLineSegment(sketch, "E102", {"start": v(122.09, 3653.63) * mm, "end": v(-108.25, 3992.06) * mm, "construction": true});
            skLineSegment(sketch, "E103", {"start": v(122.09, 3653.63) * mm, "end": v(43.9, 3768.52) * mm});
            skSolve(sketch);
        }
        {
            var Q0;
            Q0=sQuery(id+"F73.wireOp",VERTEX,"E103.end");
            var Q1;
            Q1=sQuery(id+"F73.wireOp",EDGE,"E103");
            cPlane(context, id + "F74", {"entities" : qUnion([Q0, Q1]), "cplaneType" : CPlaneType.LINE_POINT, "offset" : 25 * mm, "width" : 150 * mm, "height" : 150 * mm});
        }
        {
            var Q0;
            Q0=qCreatedBy(id+"F74.planeOp",FACE);
            var sketch = newSketch(context, id + "F75", { "sketchPlane" : qUnion([Q0])});
            skCircle(sketch, "E104", {"center": v(-2156.69, -259.55) * mm, "radius": 10 * mm});
            skCircle(sketch, "E105", {"center": v(-2156.69, -259.55) * mm, "radius": 8 * mm});
            skSolve(sketch);
        }
        {
            var Q0;
            Q0 = qSketchRegion(id + "F75", true);
            var Q1;
            Q1=makeQuery(id+"F14.opPattern","COPY",BODY,{"derivedFrom":makeQuery(id+"F11.opSweep","SWEPT_BODY",BODY,{"disambiguationData":[OSD([sQuery(id+"F7.wireOp",EDGE,"E12"),sQuery(id+"F10.wireOp",EDGE,"E13")])]}),"instanceName":"1"});
            var Q2;
            Q2=makeQuery(id+"F11.opSweep","SWEPT_BODY",BODY,{"disambiguationData":[OSD([sQuery(id+"F7.wireOp",EDGE,"E12"),sQuery(id+"F10.wireOp",EDGE,"E13")])]});
            extrude(context, id + "F76", {"entities" : qUnion([Q0]), "endBound" : BoundingType.UP_TO_BODY, "endBoundEntityBody" : qUnion([Q1]), "depth" : 25 * mm, "hasSecondDirection" : true, "secondDirectionBound" : SecondDirectionBoundingType.UP_TO_BODY, "secondDirectionOppositeDirection" : true, "secondDirectionBoundEntityBody" : qUnion([Q2]), "secondDirectionDepth" : 25 * mm});
        }
        {
            var Q0;
            Q0=makeQuery(id+"F76.opExtrude","SWEPT_BODY",BODY,{"disambiguationData":[OSD([sQuery(id+"F75.wireOp",EDGE,"E104"),sQuery(id+"F75.wireOp",EDGE,"E105")])]});
            var Q1;
            Q1=makeQuery(id+"F48.opExtrude","SWEPT_BODY",BODY,{"disambiguationData":[OSD([sQuery(id+"F47.wireOp",EDGE,"E70"),sQuery(id+"F47.wireOp",EDGE,"E71")])]});
            var Q2;
            Q2=makeQuery(id+"F72.opExtrude","SWEPT_BODY",BODY,{"disambiguationData":[OSD([sQuery(id+"F71.wireOp",EDGE,"E100"),sQuery(id+"F71.wireOp",EDGE,"E101")])]});
            var Q3;
            Q3=makeQuery(id+"F48.opExtrude","SWEPT_BODY",BODY,{"disambiguationData":[OSD([sQuery(id+"F47.wireOp",EDGE,"E69"),sQuery(id+"F47.wireOp",EDGE,"E72")])]});
            var Q4;
            Q4=makeQuery(id+"F68.opExtrude","SWEPT_BODY",BODY,{"disambiguationData":[OSD([sQuery(id+"F67.wireOp",EDGE,"E96"),sQuery(id+"F67.wireOp",EDGE,"E97")])]});
            var Q5;
            Q5=makeQuery(id+"F48.opExtrude","SWEPT_BODY",BODY,{"disambiguationData":[OSD([sQuery(id+"F47.wireOp",EDGE,"E67"),sQuery(id+"F47.wireOp",EDGE,"E73")])]});
            var Q6;
            Q6=makeQuery(id+"F64.opExtrude","SWEPT_BODY",BODY,{"disambiguationData":[OSD([sQuery(id+"F63.wireOp",EDGE,"E92"),sQuery(id+"F63.wireOp",EDGE,"E93")])]});
            var Q7;
            Q7=makeQuery(id+"F48.opExtrude","SWEPT_BODY",BODY,{"disambiguationData":[OSD([sQuery(id+"F47.wireOp",EDGE,"E66"),sQuery(id+"F47.wireOp",EDGE,"E74")])]});
            var Q8;
            Q8=makeQuery(id+"F60.opExtrude","SWEPT_BODY",BODY,{"disambiguationData":[OSD([sQuery(id+"F59.wireOp",EDGE,"E88"),sQuery(id+"F59.wireOp",EDGE,"E89")])]});
            var Q9;
            Q9=makeQuery(id+"F48.opExtrude","SWEPT_BODY",BODY,{"disambiguationData":[OSD([sQuery(id+"F47.wireOp",EDGE,"E65"),sQuery(id+"F47.wireOp",EDGE,"E75")])]});
            var Q10;
            Q10=makeQuery(id+"F56.opExtrude","SWEPT_BODY",BODY,{"disambiguationData":[OSD([sQuery(id+"F55.wireOp",EDGE,"E84"),sQuery(id+"F55.wireOp",EDGE,"E85")])]});
            var Q11;
            Q11=makeQuery(id+"F48.opExtrude","SWEPT_BODY",BODY,{"disambiguationData":[OSD([sQuery(id+"F47.wireOp",EDGE,"E64"),sQuery(id+"F47.wireOp",EDGE,"E76")])]});
            var Q12;
            Q12=makeQuery(id+"F52.opExtrude","SWEPT_BODY",BODY,{"disambiguationData":[OSD([sQuery(id+"F51.wireOp",EDGE,"E80"),sQuery(id+"F51.wireOp",EDGE,"E81")])]});
            var Q13;
            Q13=makeQuery(id+"F48.opExtrude","SWEPT_BODY",BODY,{"disambiguationData":[OSD([sQuery(id+"F47.wireOp",EDGE,"E63"),sQuery(id+"F47.wireOp",EDGE,"E77")])]});
            var Q14;
            Q14=sQuery(id+"F13.wireOp",EDGE,"E14");
            transform(context, id + "F77", {"entities" : qUnion([Q0, Q1, Q2, Q3, Q4, Q5, Q6, Q7, Q8, Q9, Q10, Q11, Q12, Q13]), "transformType" : TransformType.ROTATION, "transformAxis" : qUnion([Q14]), "angle" : 120 * degree, "makeCopy" : true});
        }
        {
            var Q0;
            Q0=makeQuery(id+"F76.opExtrude","SWEPT_BODY",BODY,{"disambiguationData":[OSD([sQuery(id+"F75.wireOp",EDGE,"E104"),sQuery(id+"F75.wireOp",EDGE,"E105")])]});
            var Q1;
            Q1=makeQuery(id+"F48.opExtrude","SWEPT_BODY",BODY,{"disambiguationData":[OSD([sQuery(id+"F47.wireOp",EDGE,"E70"),sQuery(id+"F47.wireOp",EDGE,"E71")])]});
            var Q2;
            Q2=makeQuery(id+"F72.opExtrude","SWEPT_BODY",BODY,{"disambiguationData":[OSD([sQuery(id+"F71.wireOp",EDGE,"E100"),sQuery(id+"F71.wireOp",EDGE,"E101")])]});
            var Q3;
            Q3=makeQuery(id+"F48.opExtrude","SWEPT_BODY",BODY,{"disambiguationData":[OSD([sQuery(id+"F47.wireOp",EDGE,"E69"),sQuery(id+"F47.wireOp",EDGE,"E72")])]});
            var Q4;
            Q4=makeQuery(id+"F68.opExtrude","SWEPT_BODY",BODY,{"disambiguationData":[OSD([sQuery(id+"F67.wireOp",EDGE,"E96"),sQuery(id+"F67.wireOp",EDGE,"E97")])]});
            var Q5;
            Q5=makeQuery(id+"F48.opExtrude","SWEPT_BODY",BODY,{"disambiguationData":[OSD([sQuery(id+"F47.wireOp",EDGE,"E67"),sQuery(id+"F47.wireOp",EDGE,"E73")])]});
            var Q6;
            Q6=makeQuery(id+"F64.opExtrude","SWEPT_BODY",BODY,{"disambiguationData":[OSD([sQuery(id+"F63.wireOp",EDGE,"E92"),sQuery(id+"F63.wireOp",EDGE,"E93")])]});
            var Q7;
            Q7=makeQuery(id+"F48.opExtrude","SWEPT_BODY",BODY,{"disambiguationData":[OSD([sQuery(id+"F47.wireOp",EDGE,"E66"),sQuery(id+"F47.wireOp",EDGE,"E74")])]});
            var Q8;
            Q8=makeQuery(id+"F60.opExtrude","SWEPT_BODY",BODY,{"disambiguationData":[OSD([sQuery(id+"F59.wireOp",EDGE,"E88"),sQuery(id+"F59.wireOp",EDGE,"E89")])]});
            var Q9;
            Q9=makeQuery(id+"F48.opExtrude","SWEPT_BODY",BODY,{"disambiguationData":[OSD([sQuery(id+"F47.wireOp",EDGE,"E65"),sQuery(id+"F47.wireOp",EDGE,"E75")])]});
            var Q10;
            Q10=makeQuery(id+"F56.opExtrude","SWEPT_BODY",BODY,{"disambiguationData":[OSD([sQuery(id+"F55.wireOp",EDGE,"E84"),sQuery(id+"F55.wireOp",EDGE,"E85")])]});
            var Q11;
            Q11=makeQuery(id+"F48.opExtrude","SWEPT_BODY",BODY,{"disambiguationData":[OSD([sQuery(id+"F47.wireOp",EDGE,"E64"),sQuery(id+"F47.wireOp",EDGE,"E76")])]});
            var Q12;
            Q12=makeQuery(id+"F52.opExtrude","SWEPT_BODY",BODY,{"disambiguationData":[OSD([sQuery(id+"F51.wireOp",EDGE,"E80"),sQuery(id+"F51.wireOp",EDGE,"E81")])]});
            var Q13;
            Q13=makeQuery(id+"F48.opExtrude","SWEPT_BODY",BODY,{"disambiguationData":[OSD([sQuery(id+"F47.wireOp",EDGE,"E63"),sQuery(id+"F47.wireOp",EDGE,"E77")])]});
            var Q14;
            Q14=sQuery(id+"F13.wireOp",EDGE,"E14");
            transform(context, id + "F78", {"entities" : qUnion([Q0, Q1, Q2, Q3, Q4, Q5, Q6, Q7, Q8, Q9, Q10, Q11, Q12, Q13]), "transformType" : TransformType.ROTATION, "transformAxis" : qUnion([Q14]), "angle" : 120 * degree, "oppositeDirection" : true, "makeCopy" : true});
        }
        {
            var Q0;
            Q0=makeQuery(id+"F17.opExtrude","CAP_FACE",FACE,{"disambiguationData":[OSD([sQuery(id+"F16.wireOp",EDGE,"E15")])],"isStart":false});
            var sketch = newSketch(context, id + "F79", { "sketchPlane" : qUnion([Q0])});
            skCircle(sketch, "E106.cCircle", {"center": v(0, 0) * mm, "radius": 86.6 * mm, "construction": true});
            skLineSegment(sketch, "E106.0", {"start": v(50, 86.6) * mm, "end": v(100, 0) * mm});
            skLineSegment(sketch, "E106.1", {"start": v(100, 0) * mm, "end": v(50, -86.6) * mm});
            skLineSegment(sketch, "E106.2", {"start": v(50, -86.6) * mm, "end": v(-50, -86.6) * mm});
            skLineSegment(sketch, "E106.3", {"start": v(-50, -86.6) * mm, "end": v(-100, 0) * mm});
            skLineSegment(sketch, "E106.4", {"start": v(-100, 0) * mm, "end": v(-50, 86.6) * mm});
            skLineSegment(sketch, "E106.5", {"start": v(-50, 86.6) * mm, "end": v(50, 86.6) * mm});
            skPoint(sketch, "E106.0.midPoint", {"position": v(75, 43.3) * mm});
            skSolve(sketch);
        }
        {
            var Q0;
            Q0 = qSketchRegion(id + "F79", true);
            extrude(context, id + "F80", {"entities" : qUnion([Q0]), "operationType" : NewBodyOperationType.ADD, "depth" : 100 * mm});
        }
    });
